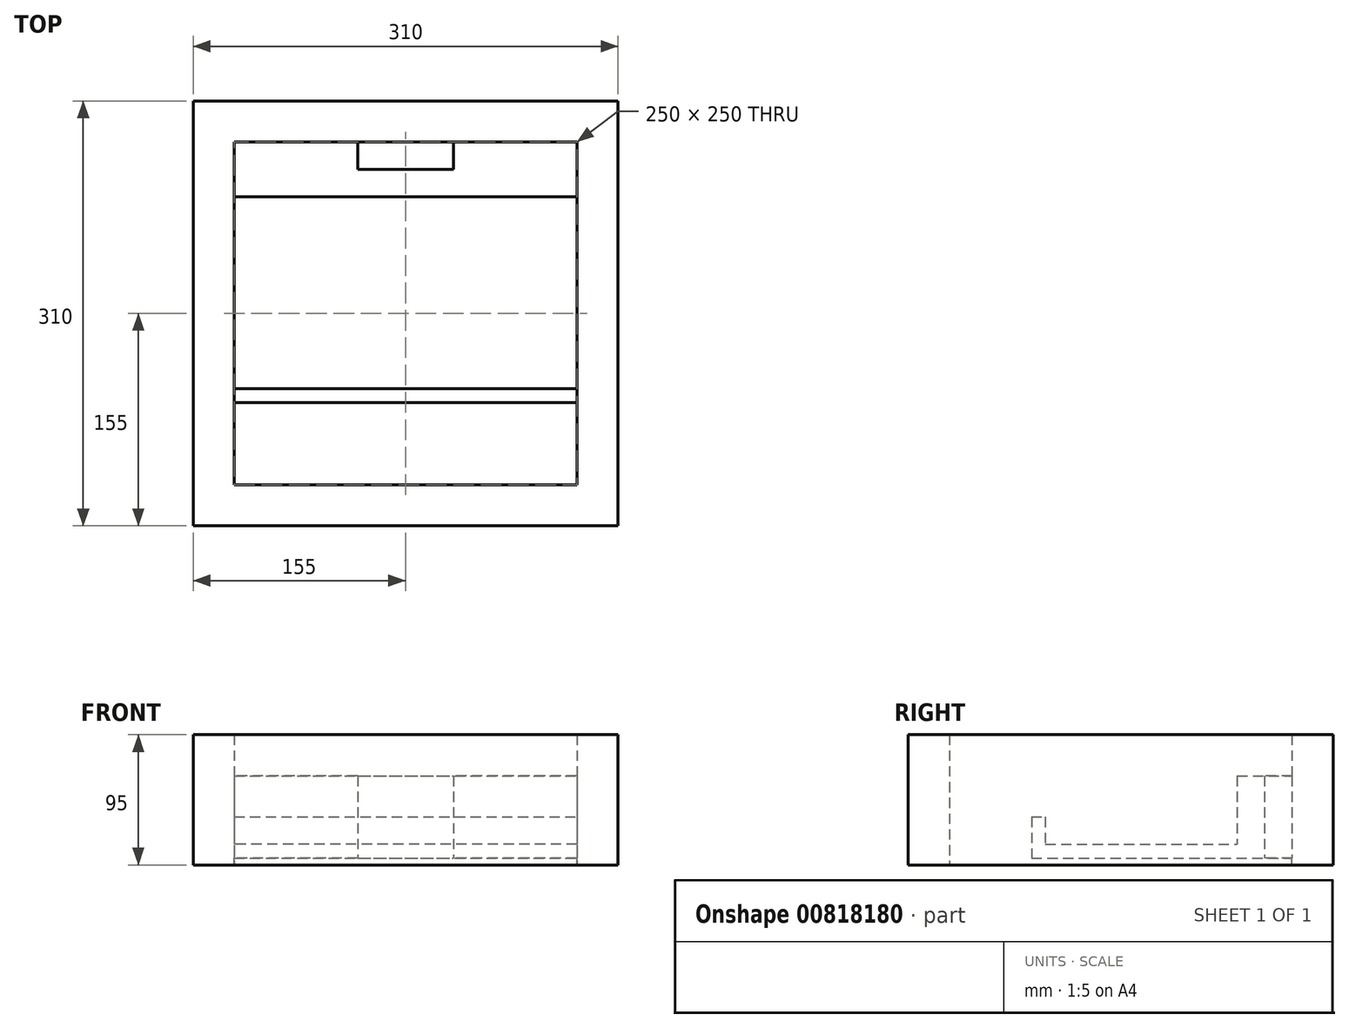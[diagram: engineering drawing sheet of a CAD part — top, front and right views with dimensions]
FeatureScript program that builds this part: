
annotation { "Feature Type Name" : "Feature", "Feature Type Description" : "" }
export const myFeature = defineFeature(function(context is Context, id is Id, definition is map)
    precondition{}
    {
        {
            var Q0;
            Q0=qCreatedBy(makeId("Top.planeOp"),FACE);
            var sketch = newSketch(context, id + "F0", { "sketchPlane" : qUnion([Q0])});
            skLineSegment(sketch, "E0.bottom", {"start": v(155, -155) * mm, "end": v(-155, -155) * mm});
            skLineSegment(sketch, "E0.top", {"start": v(155, 155) * mm, "end": v(-155, 155) * mm});
            skLineSegment(sketch, "E0.left", {"start": v(155, -155) * mm, "end": v(155, 155) * mm});
            skLineSegment(sketch, "E0.right", {"start": v(-155, -155) * mm, "end": v(-155, 155) * mm});
            skPoint(sketch, "E0.middle", {"position": v(0, 0) * mm});
            skLineSegment(sketch, "E1.bottom", {"start": v(125, -125) * mm, "end": v(-125, -125) * mm});
            skLineSegment(sketch, "E1.top", {"start": v(125, 125) * mm, "end": v(-125, 125) * mm});
            skLineSegment(sketch, "E1.left", {"start": v(125, -125) * mm, "end": v(125, 125) * mm});
            skLineSegment(sketch, "E1.right", {"start": v(-125, -125) * mm, "end": v(-125, 125) * mm});
            skSolve(sketch);
        }
        {
            var Q0;
            Q0=makeQuery(id+"F0.imprint","IMPRINT",FACE,{"disambiguationData":[TD([[makeQuery(id+"F0.imprint","IMPRINT",EDGE,{"derivedFrom":sQuery(id+"F0.wireOp",EDGE,"E0.bottom")}),-1.0]])]});
            extrude(context, id + "F1", {"entities" : qUnion([Q0]), "depth" : 90 * mm, "offsetDistance" : 25 * mm});
        }
        {
            var Q0;
            Q0=makeQuery(id+"F1.opExtrude","CAP_FACE",FACE,{"disambiguationData":[OSD([sQuery(id+"F0.wireOp",EDGE,"E0.bottom"),sQuery(id+"F0.wireOp",EDGE,"E0.top"),sQuery(id+"F0.wireOp",EDGE,"E0.left"),sQuery(id+"F0.wireOp",EDGE,"E0.right"),sQuery(id+"F0.wireOp",EDGE,"E1.bottom"),sQuery(id+"F0.wireOp",EDGE,"E1.top"),sQuery(id+"F0.wireOp",EDGE,"E1.left"),sQuery(id+"F0.wireOp",EDGE,"E1.right")])],"isStart":true});
            var sketch = newSketch(context, id + "F2", { "sketchPlane" : qUnion([Q0])});
            skLineSegment(sketch, "E2", {"start": v(-125, -125) * mm, "end": v(-125, -85) * mm});
            skLineSegment(sketch, "E3", {"start": v(-125, -85) * mm, "end": v(125, -85) * mm});
            skLineSegment(sketch, "E4", {"start": v(125, -85) * mm, "end": v(125, -125) * mm});
            skLineSegment(sketch, "E5", {"start": v(125, -125) * mm, "end": v(-125, -125) * mm});
            skLineSegment(sketch, "E6", {"start": v(-35, -125) * mm, "end": v(-35, -105) * mm});
            skLineSegment(sketch, "E7", {"start": v(-35, -105) * mm, "end": v(35, -105) * mm});
            skLineSegment(sketch, "E8", {"start": v(35, -105) * mm, "end": v(35, -125) * mm});
            skLineSegment(sketch, "E9", {"start": v(35, -125) * mm, "end": v(-35, -125) * mm});
            skSolve(sketch);
        }
        {
            var Q0;
            {var subQ4=sQuery(id+"F2.wireOp",EDGE,"E2");Q0=makeQuery(id+"F2.imprint","IMPRINT",FACE,{"disambiguationData":[TD([[makeQuery(id+"F2.imprint","IMPRINT",EDGE,{"derivedFrom":subQ4}),1.0]])]});}
            extrude(context, id + "F3", {"entities" : qUnion([Q0]), "operationType" : NewBodyOperationType.ADD, "oppositeDirection" : true, "depth" : 60 * mm, "offsetDistance" : 25 * mm});
        }
        {
            var Q0;
            Q0=makeQuery(id+"F3.boolean.opBoolean","MERGE",FACE,{"derivedFrom":[makeQuery(id+"F1.opExtrude","CAP_FACE",FACE,{"disambiguationData":[OSD([sQuery(id+"F0.wireOp",EDGE,"E0.bottom"),sQuery(id+"F0.wireOp",EDGE,"E0.top"),sQuery(id+"F0.wireOp",EDGE,"E0.left"),sQuery(id+"F0.wireOp",EDGE,"E0.right"),sQuery(id+"F0.wireOp",EDGE,"E1.bottom"),sQuery(id+"F0.wireOp",EDGE,"E1.top"),sQuery(id+"F0.wireOp",EDGE,"E1.left"),sQuery(id+"F0.wireOp",EDGE,"E1.right")])],"isStart":true}),makeQuery(id+"F3.opExtrude","CAP_FACE",FACE,{"disambiguationData":[OSD([sQuery(id+"F2.wireOp",EDGE,"E2"),sQuery(id+"F2.wireOp",EDGE,"E3"),sQuery(id+"F2.wireOp",EDGE,"E4"),sQuery(id+"F2.wireOp",EDGE,"E5"),sQuery(id+"F2.wireOp",EDGE,"E6"),sQuery(id+"F2.wireOp",EDGE,"E7"),sQuery(id+"F2.wireOp",EDGE,"E8")])],"isStart":true})]});
            var sketch = newSketch(context, id + "F4", { "sketchPlane" : qUnion([Q0])});
            skLineSegment(sketch, "E10", {"start": v(125, 125) * mm, "end": v(-125, 125) * mm});
            skLineSegment(sketch, "E11", {"start": v(-125, 125) * mm, "end": v(-125, -85) * mm});
            skLineSegment(sketch, "E12", {"start": v(-125, -85) * mm, "end": v(125, -85) * mm});
            skLineSegment(sketch, "E13", {"start": v(125, -85) * mm, "end": v(125, 55) * mm});
            skLineSegment(sketch, "E14", {"start": v(125, 55) * mm, "end": v(-125, 55) * mm});
            skLineSegment(sketch, "E15", {"start": v(-125, 55) * mm, "end": v(-125, -85) * mm});
            skLineSegment(sketch, "E16", {"start": v(125, 125) * mm, "end": v(125, 55) * mm});
            skLineSegment(sketch, "E17", {"start": v(-125, 55) * mm, "end": v(-125, 65) * mm});
            skLineSegment(sketch, "E18", {"start": v(-125, 65) * mm, "end": v(125, 65) * mm});
            skLineSegment(sketch, "E19", {"start": v(125, 65) * mm, "end": v(125, 55) * mm});
            skSolve(sketch);
        }
        {
            var Q0;
            Q0=makeQuery(id+"F4.imprint","IMPRINT",FACE,{"disambiguationData":[TD([[makeQuery(id+"F4.imprint","IMPRINT",EDGE,{"derivedFrom":sQuery(id+"F4.wireOp",EDGE,"E12")}),1.0]])]});
            var Q1;
            Q1=makeQuery(id+"F4.imprint","IMPRINT",FACE,{"disambiguationData":[TD([[makeQuery(id+"F4.imprint","IMPRINT",EDGE,{"derivedFrom":sQuery(id+"F4.wireOp",EDGE,"E14")}),-1.0]])]});
            extrude(context, id + "F5", {"entities" : qUnion([Q0, Q1]), "operationType" : NewBodyOperationType.ADD, "oppositeDirection" : true, "depth" : 10 * mm, "offsetDistance" : 25 * mm});
        }
        {
            var Q0;
            Q0=makeQuery(id+"F4.imprint","IMPRINT",FACE,{"disambiguationData":[TD([[makeQuery(id+"F4.imprint","IMPRINT",EDGE,{"derivedFrom":sQuery(id+"F4.wireOp",EDGE,"E14")}),-1.0]])]});
            extrude(context, id + "F6", {"entities" : qUnion([Q0]), "operationType" : NewBodyOperationType.ADD, "oppositeDirection" : true, "depth" : 30 * mm, "offsetDistance" : 25 * mm});
        }
        {
            var Q0;
            Q0 = qSketchRegion(id + "F0", true);
            extrude(context, id + "F7", {"entities" : qUnion([Q0]), "operationType" : NewBodyOperationType.ADD, "oppositeDirection" : true, "depth" : 5 * mm, "offsetDistance" : 25 * mm});
        }
    });
